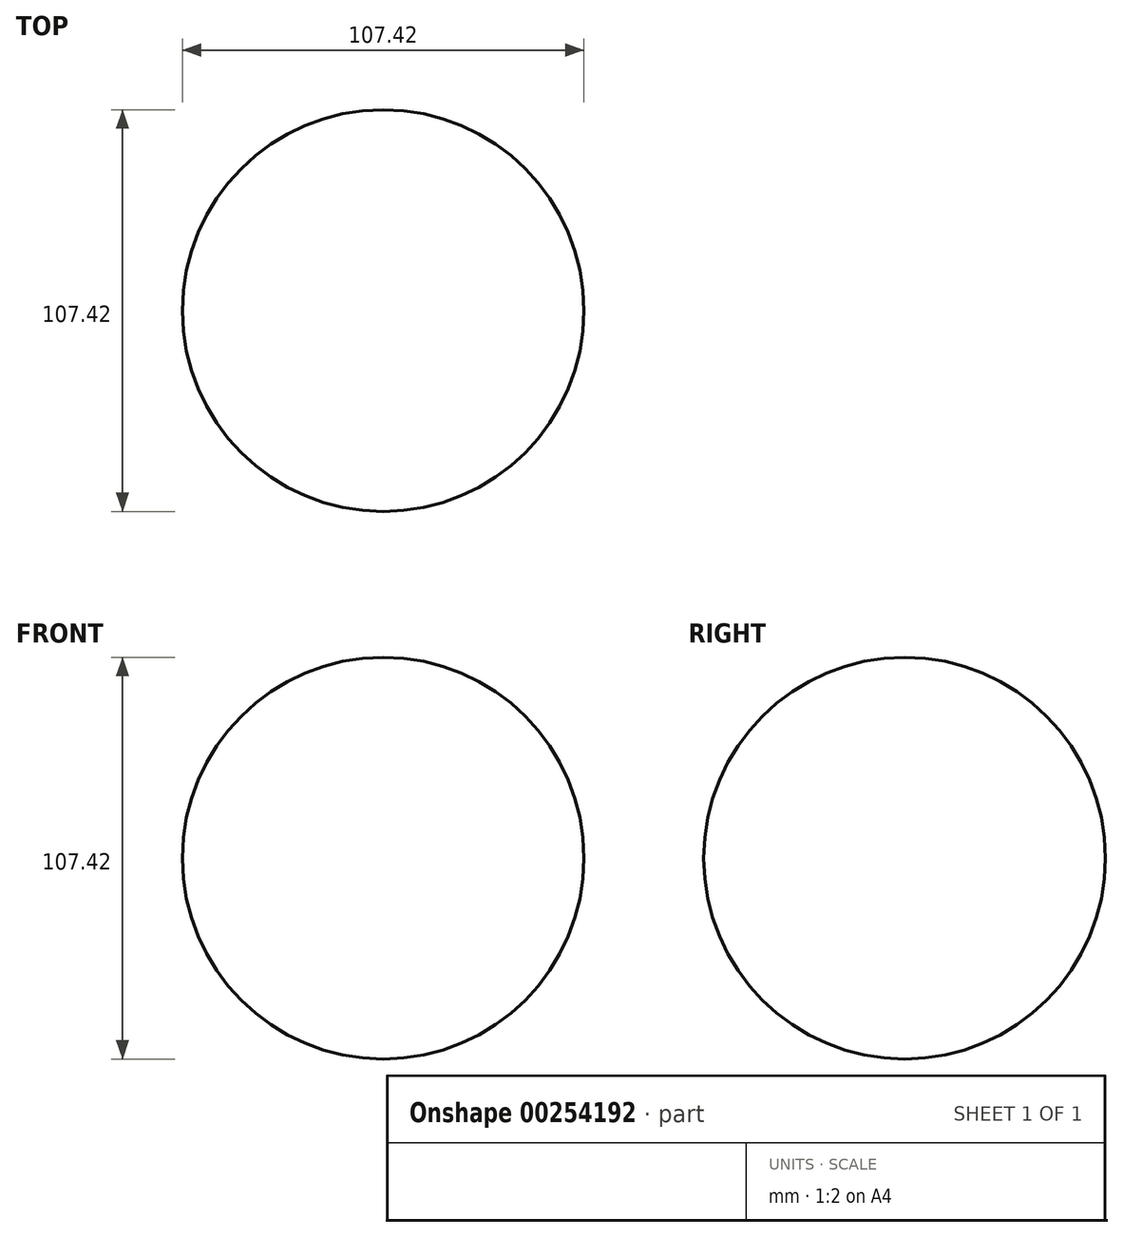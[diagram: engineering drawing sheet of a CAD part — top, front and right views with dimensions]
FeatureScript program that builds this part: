
annotation { "Feature Type Name" : "Feature", "Feature Type Description" : "" }
export const myFeature = defineFeature(function(context is Context, id is Id, definition is map)
    precondition{}
    {
        {
            var Q0;
            Q0=qCreatedBy(makeId("Front.planeOp"),FACE);
            var sketch = newSketch(context, id + "F0", { "sketchPlane" : qUnion([Q0])});
            skLineSegment(sketch, "E0", {"start": v(0, 75.74) * mm, "end": v(0, -76.77) * mm, "construction": true});
            skArc(sketch, "E1", {"start": v(0, 53.7) * mm, "mid": v(-53.7, 0) * mm, "end": v(0, -53.7) * mm});
            skLineSegment(sketch, "E2", {"start": v(0, -53.7) * mm, "end": v(0, 53.7) * mm});
            skSolve(sketch);
        }
        {
            var Q0;
            Q0=makeQuery(id+"F0.imprint","IMPRINT",FACE,{"disambiguationData":[TD([[makeQuery(id+"F0.imprint","IMPRINT",EDGE,{"derivedFrom":sQuery(id+"F0.wireOp",EDGE,"E1")}),1.0]])]});
            var Q1;
            Q1=sQuery(id+"F0.wireOp",EDGE,"E2");
            revolve(context, id + "F1", {"entities" : qUnion([Q0]), "axis" : qUnion([Q1]), "revolveType" : RevolveType.FULL});
        }
    });
